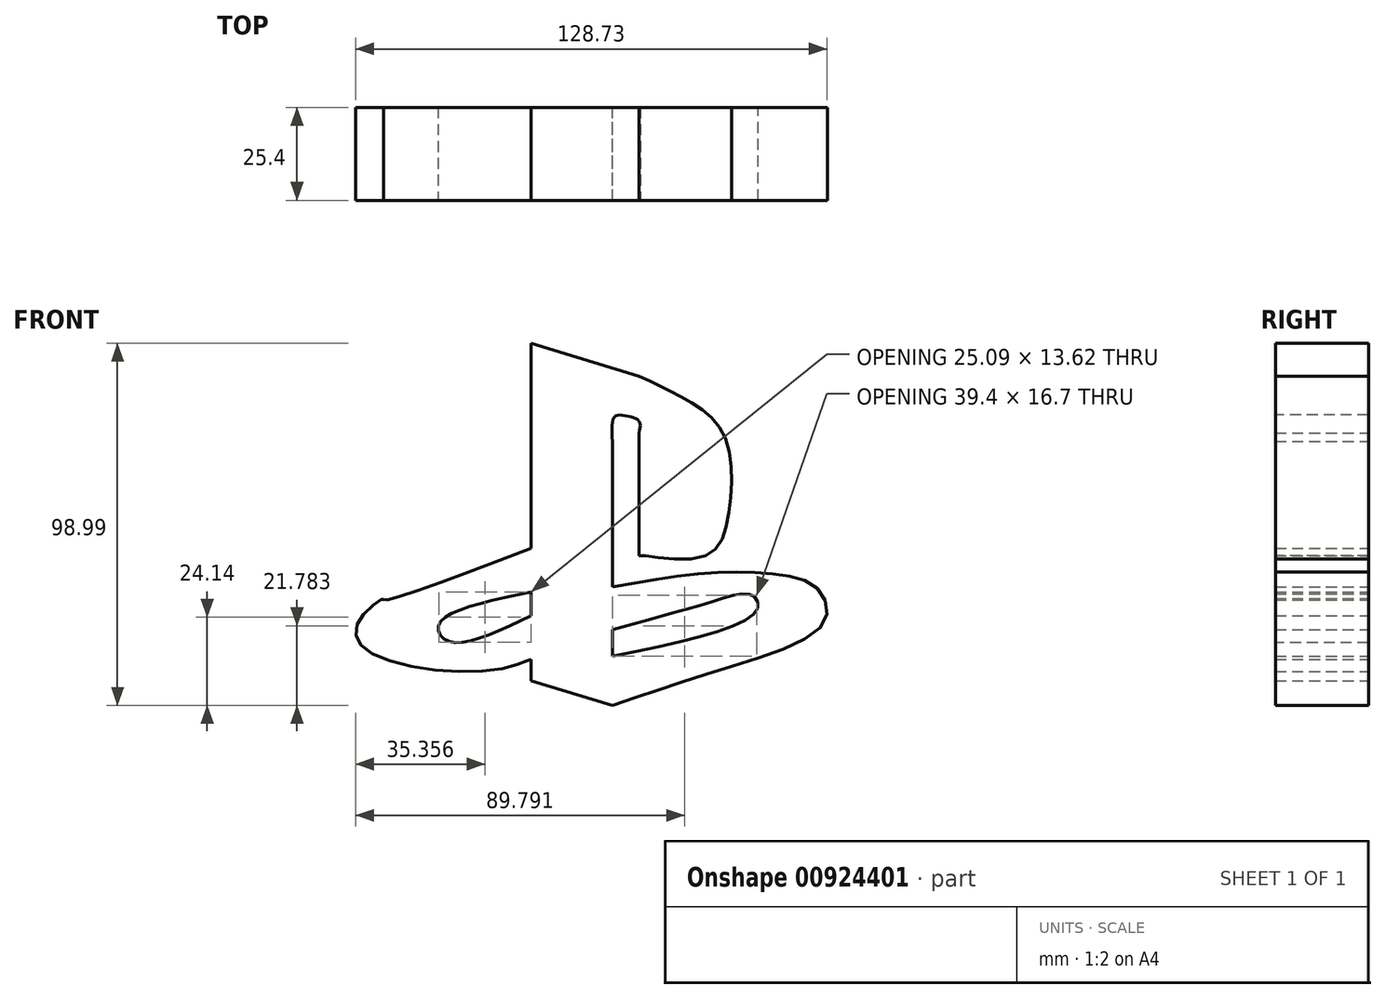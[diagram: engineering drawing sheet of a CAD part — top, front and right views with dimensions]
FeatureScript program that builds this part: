
annotation { "Feature Type Name" : "Feature", "Feature Type Description" : "" }
export const myFeature = defineFeature(function(context is Context, id is Id, definition is map)
    precondition{}
    {
        {
            var Q0;
            Q0=qCreatedBy(makeId("Front.planeOp"),FACE);
            var sketch = newSketch(context, id + "F0", { "sketchPlane" : qUnion([Q0])});
            skLineSegment(sketch, "E0", {"start": v(-15.33, -46.58) * mm, "end": v(-15.33, 45.7) * mm});
            skLineSegment(sketch, "E1", {"start": v(-15.33, 45.7) * mm, "end": v(14.16, 36.65) * mm});
            skFitSpline(sketch, "E2", {"points": [v(14.16, 36.65) * mm, v(26.13, 30.8) * mm, v(37.23, 20.88) * mm, v(38.7, 0) * mm, v(31.4, -12.7) * mm, v(14.16, -12.41) * mm, v(14.16, -12.7) * mm], "startDerivative": vector(66.78, -30.5) * mm, "endDerivative": vector(6.3, -13.06) * mm});
            skLineSegment(sketch, "E3", {"start": v(14.16, -12.41) * mm, "end": v(14.16, 21.17) * mm});
            skFitSpline(sketch, "E4", {"points": [v(14.16, 21.17) * mm, v(14.16, 24.38) * mm, v(10.66, 25.84) * mm, v(7.45, 25.55) * mm, v(6.86, 18.83) * mm], "startDerivative": vector(3.6, 16.52) * mm, "endDerivative": vector(1.83, -26.77) * mm});
            skLineSegment(sketch, "E5", {"start": v(6.86, 18.83) * mm, "end": v(6.86, -53.3) * mm});
            skLineSegment(sketch, "E6", {"start": v(6.86, -53.3) * mm, "end": v(-15.33, -46.58) * mm});
            skFitSpline(sketch, "E7", {"points": [v(-15.33, -10.37) * mm, v(-55.63, -24.38) * mm, v(-55.63, -24.1) * mm, v(-62.05, -29.64) * mm, v(-60.3, -38.1) * mm, v(-23.8, -43.36) * mm, v(-15.33, -40.74) * mm, v(-15.33, -41.03) * mm], "startDerivative": vector(-205.7, -78.3) * mm, "endDerivative": vector(-3.7, -15.2) * mm});
            skFitSpline(sketch, "E8", {"points": [v(-15.33, -22.34) * mm, v(-40.44, -31.1) * mm, v(-37.81, -35.77) * mm, v(-15.33, -28.76) * mm], "startDerivative": vector(-83.75, -17.1) * mm, "endDerivative": vector(68.1, 32.83) * mm});
            skPoint(sketch, "E9.1.internal.snap0", {"position": v(6.86, -17.23) * mm});
            skPoint(sketch, "E9.2.internal.snap0", {"position": v(6.86, -17.23) * mm});
            skFitSpline(sketch, "E9", {"points": [v(6.86, -20.88) * mm, v(31.4, -17.23) * mm, v(49.79, -17.23) * mm, v(62.64, -21.17) * mm, v(64.68, -30.51) * mm, v(38.7, -42.78) * mm, v(6.86, -53.3) * mm], "startDerivative": vector(138.22, 24.55) * mm, "endDerivative": vector(-142.05, -48.67) * mm});
            skFitSpline(sketch, "E10", {"points": [v(6.86, -32.56) * mm, v(34.9, -24.67) * mm, v(45.12, -23.21) * mm, v(46.28, -27.3) * mm, v(6.86, -39.86) * mm], "startDerivative": vector(97.11, 26.38) * mm, "endDerivative": vector(-146.22, -30.09) * mm});
            skSolve(sketch);
        }
        {
            var Q0;
            Q0 = qSketchRegion(id + "F0", true);
            extrude(context, id + "F1", {"entities" : qUnion([Q0]), "depth" : 25.4 * mm, "offsetDistance" : 25.4 * mm});
        }
    });
